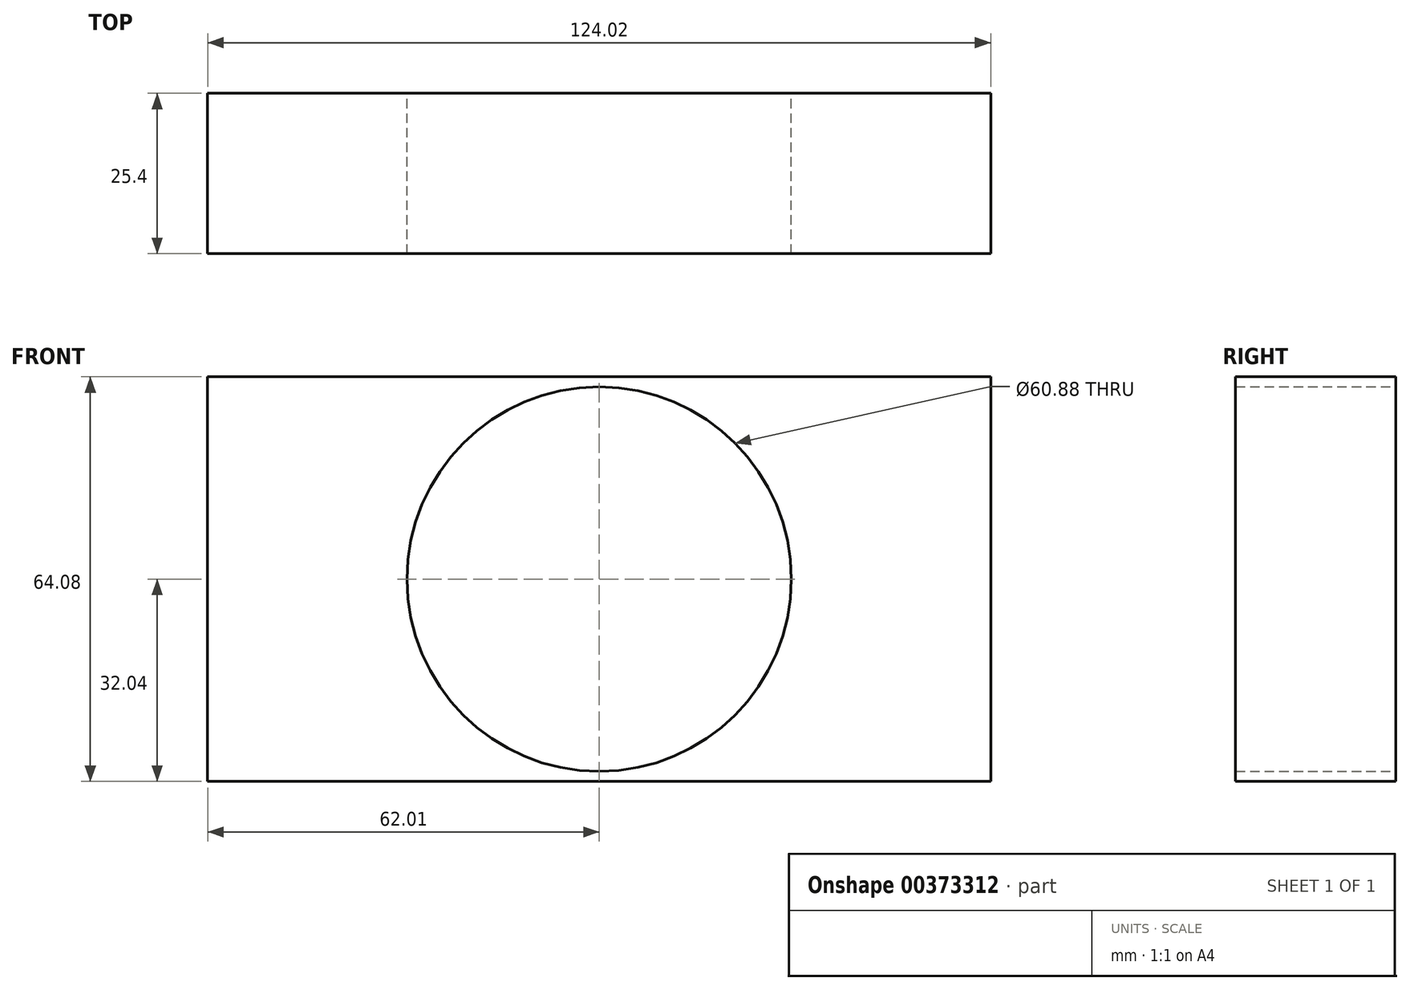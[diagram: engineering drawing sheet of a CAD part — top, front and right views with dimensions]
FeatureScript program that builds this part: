
annotation { "Feature Type Name" : "Feature", "Feature Type Description" : "" }
export const myFeature = defineFeature(function(context is Context, id is Id, definition is map)
    precondition{}
    {
        {
            var Q0;
            Q0=qCreatedBy(makeId("Front.planeOp"),FACE);
            var sketch = newSketch(context, id + "F0", { "sketchPlane" : qUnion([Q0])});
            skLineSegment(sketch, "E0.bottom", {"start": v(62.01, -32.04) * mm, "end": v(-62.01, -32.04) * mm});
            skLineSegment(sketch, "E0.top", {"start": v(62.01, 32.04) * mm, "end": v(-62.01, 32.04) * mm});
            skLineSegment(sketch, "E0.left", {"start": v(62.01, -32.04) * mm, "end": v(62.01, 32.04) * mm});
            skLineSegment(sketch, "E0.right", {"start": v(-62.01, -32.04) * mm, "end": v(-62.01, 32.04) * mm});
            skPoint(sketch, "E0.middle", {"position": v(0, 0) * mm});
            skCircle(sketch, "E1", {"center": v(0, 0) * mm, "radius": 30.44 * mm});
            skSolve(sketch);
        }
        {
            var Q0;
            Q0 = qSketchRegion(id + "F0", true);
            extrude(context, id + "F1", {"entities" : qUnion([Q0]), "depth" : 25.4 * mm});
        }
    });
